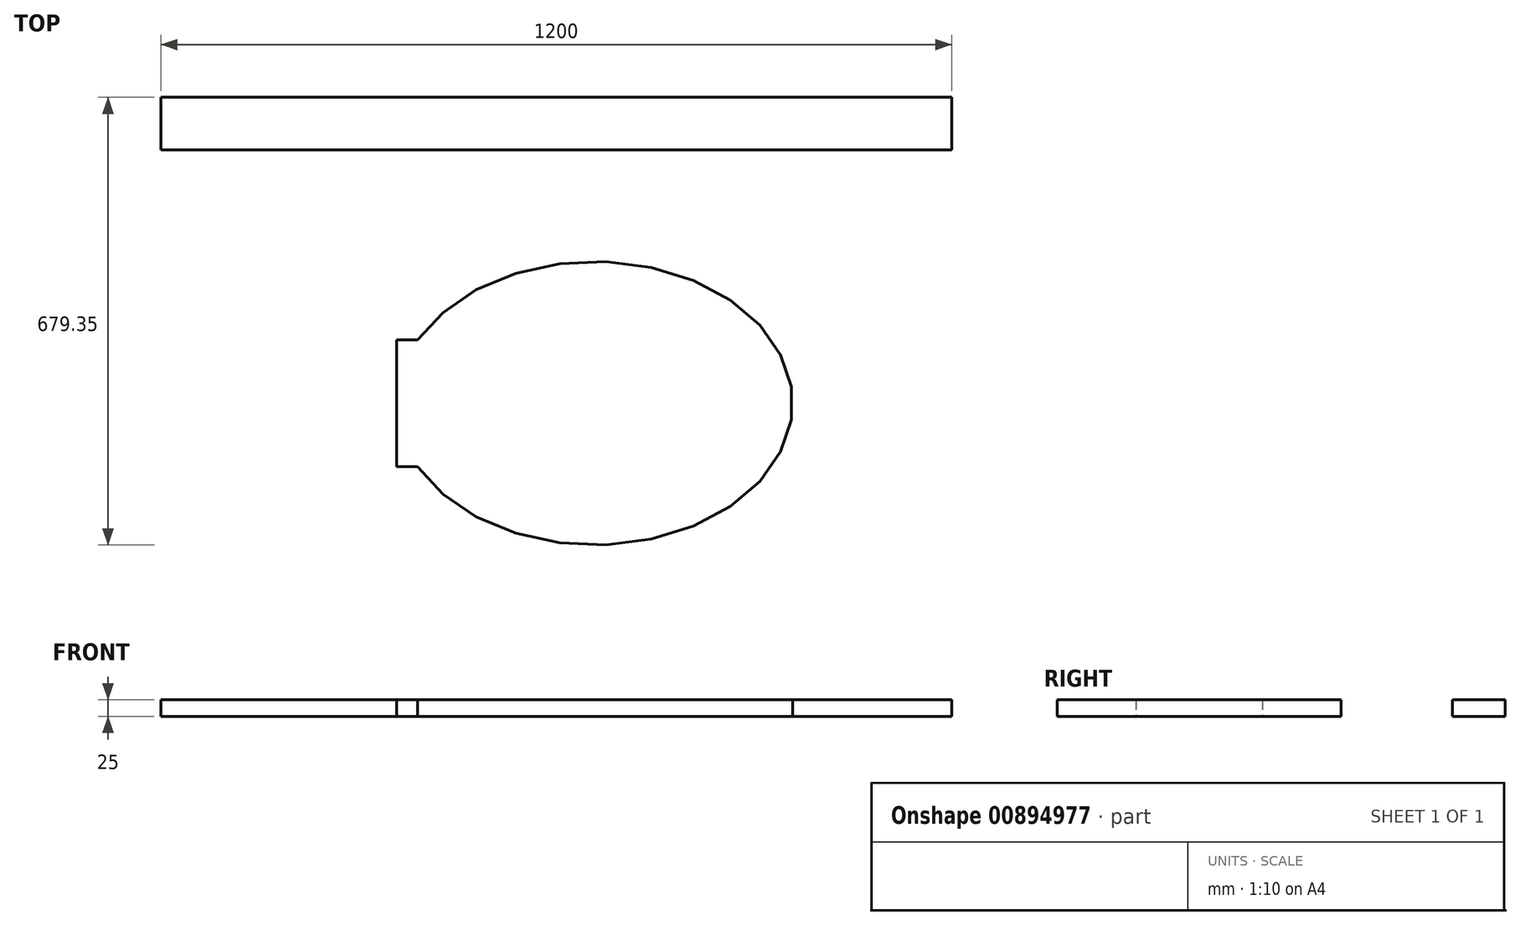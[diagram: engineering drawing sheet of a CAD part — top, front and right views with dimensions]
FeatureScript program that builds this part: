
annotation { "Feature Type Name" : "Feature", "Feature Type Description" : "" }
export const myFeature = defineFeature(function(context is Context, id is Id, definition is map)
    precondition{}
    {
        {
            var Q0;
            Q0=qCreatedBy(makeId("Top.planeOp"),FACE);
            var sketch = newSketch(context, id + "F0", { "sketchPlane" : qUnion([Q0])});
            skLineSegment(sketch, "E0.bottom", {"start": v(-658.24, 464.35) * mm, "end": v(541.76, 464.35) * mm});
            skLineSegment(sketch, "E0.top", {"start": v(-658.24, 384.35) * mm, "end": v(541.76, 384.35) * mm});
            skLineSegment(sketch, "E0.left", {"start": v(-658.24, 464.35) * mm, "end": v(-658.24, 384.35) * mm});
            skLineSegment(sketch, "E0.right", {"start": v(541.76, 464.35) * mm, "end": v(541.76, 384.35) * mm});
            skSolve(sketch);
        }
        {
            var Q0;
            Q0 = qSketchRegion(id + "F0", true);
            extrude(context, id + "F1", {"entities" : qUnion([Q0]), "depth" : 25 * mm, "offsetDistance" : 25 * mm});
        }
        {
            var Q0;
            Q0=qCreatedBy(makeId("Top.planeOp"),FACE);
            var sketch = newSketch(context, id + "F2", { "sketchPlane" : qUnion([Q0])});
            skEllipticalArc(sketch, "E1", {});
            skPoint(sketch, "E2", {"position": v(-300.43, 0) * mm});
            skPoint(sketch, "E2.positionSnap0", {"position": v(-300, 0) * mm});
            skLineSegment(sketch, "E3", {"start": v(-300.43, 96) * mm, "end": v(-300.43, -96) * mm});
            skLineSegment(sketch, "E4", {"start": v(-300.43, 96) * mm, "end": v(-268.43, 96) * mm});
            skLineSegment(sketch, "E5", {"start": v(-300.43, -96) * mm, "end": v(-268.43, -96) * mm});
            skPoint(sketch, "E6", {"position": v(0, 215) * mm});
            skPoint(sketch, "E7", {"position": v(300, 0) * mm});
            skPoint(sketch, "E8", {"position": v(0, -215) * mm});
            const initialGuessF2  = {"E1": [0, 0, -1, 0, 0.3, 0.215, 0.4628629392189901, 5.820322367960596]};
            skSetInitialGuess(sketch, initialGuessF2);
            skSolve(sketch);
        }
        {
            var Q0;
            Q0 = qSketchRegion(id + "F2", true);
            extrude(context, id + "F3", {"entities" : qUnion([Q0]), "depth" : 25 * mm, "offsetDistance" : 25 * mm});
        }
    });
